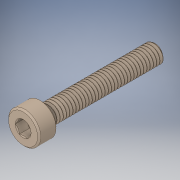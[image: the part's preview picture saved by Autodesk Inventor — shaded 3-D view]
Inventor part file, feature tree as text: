
AUTODESK INVENTOR PART (.ipt)
format: ipt  version: 2019 (Build 230136000, 136)  size: 625,152 bytes
history: mixed  units: mm
features: chamfer x1, imported_body x1
ambient origin geometry x8: Origin, YZ Plane, XZ Plane, XY Plane, X Axis, Y Axis, Z Axis, Center Point
bodies: Solid1 (imported_parasolid)
feature tree (2):
  chamfer  "Chamfer1"  [1 undecoded]
  imported_body  NMx_Import_Brep_tag  [imported B-rep: ~3 faces, bbox_mm=None]
note: 1 required parameter value undecoded (feature->parameter linkage not recoverable at this tier; creation-order binding heuristic only, values carry confidence <= 0.55)
